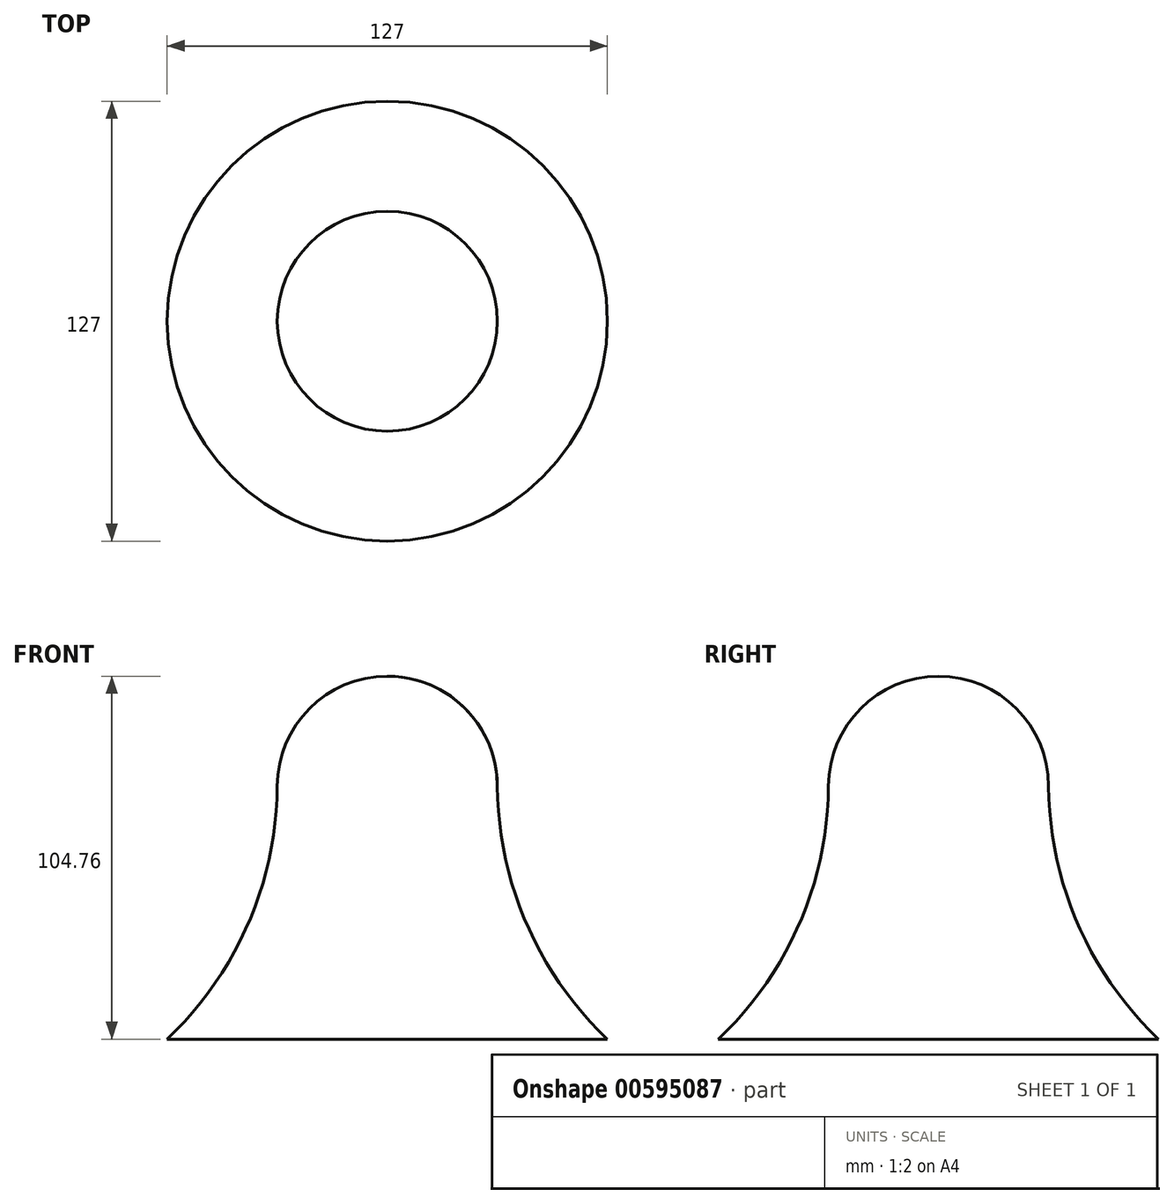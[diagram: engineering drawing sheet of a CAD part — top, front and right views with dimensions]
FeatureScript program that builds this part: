
annotation { "Feature Type Name" : "Feature", "Feature Type Description" : "" }
export const myFeature = defineFeature(function(context is Context, id is Id, definition is map)
    precondition{}
    {
        {
            var Q0;
            Q0=qCreatedBy(makeId("Front.planeOp"),FACE);
            var sketch = newSketch(context, id + "F0", { "sketchPlane" : qUnion([Q0])});
            skArc(sketch, "E0", {"start": v(0, 31.75) * mm, "mid": v(-31.75, 0) * mm, "end": v(0, -31.75) * mm});
            skArc(sketch, "E1", {"start": v(-63.5, -73.01) * mm, "mid": v(-40.18, -39.75) * mm, "end": v(-31.75, 0) * mm});
            skLineSegment(sketch, "E2", {"start": v(-63.5, -73.01) * mm, "end": v(0, -73.01) * mm});
            skLineSegment(sketch, "E3", {"start": v(0, -73.01) * mm, "end": v(0, 31.75) * mm});
            skSolve(sketch);
        }
        {
            var Q0;
            {var subQ0=sQuery(id+"F0.wireOp",EDGE,"E3");var subQ1=sQuery(id+"F0.wireOp",EDGE,"E0");var subQ2=makeQuery(id+"F0.imprint","INTERSECT",VERTEX,{"disambiguationData":[OD(0.0)],"derivedFrom":[subQ1,subQ0]});Q0=makeQuery(id+"F0.imprint","IMPRINT",FACE,{"disambiguationData":[TD([[makeQuery(id+"F0.imprint","IMPRINT",EDGE,{"disambiguationData":[TD([[subQ2,-1.0]])],"derivedFrom":subQ1}),1.0]])]});}
            var Q1;
            {var subQ3=sQuery(id+"F0.wireOp",EDGE,"E1");Q1=makeQuery(id+"F0.imprint","IMPRINT",FACE,{"disambiguationData":[TD([[makeQuery(id+"F0.imprint","IMPRINT",EDGE,{"derivedFrom":subQ3}),-1.0]])]});}
            var Q2;
            Q2=sQuery(id+"F0.wireOp",EDGE,"E3");
            revolve(context, id + "F1", {"entities" : qUnion([Q0, Q1]), "axis" : qUnion([Q2]), "revolveType" : RevolveType.FULL, "oppositeDirection" : true});
        }
    });
